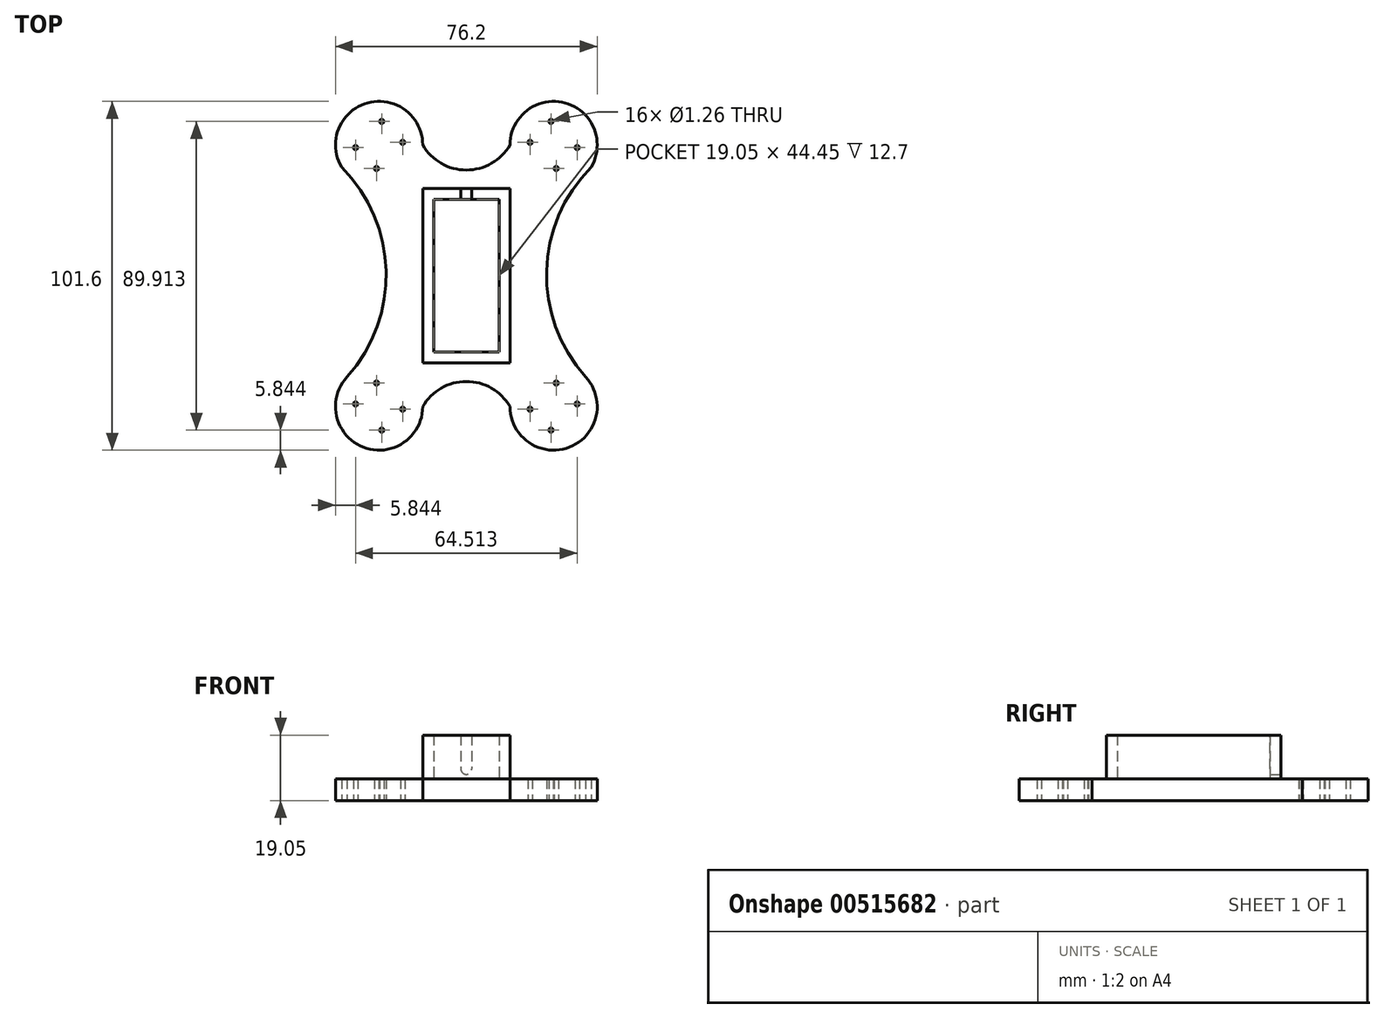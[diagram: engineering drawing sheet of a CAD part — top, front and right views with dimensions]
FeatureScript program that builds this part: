
annotation { "Feature Type Name" : "Feature", "Feature Type Description" : "" }
export const myFeature = defineFeature(function(context is Context, id is Id, definition is map)
    precondition{}
    {
        {
            var Q0;
            Q0=qCreatedBy(makeId("Top.planeOp"),FACE);
            var sketch = newSketch(context, id + "F0", { "sketchPlane" : qUnion([Q0])});
            skCircle(sketch, "E0", {"center": v(-25.4, 38.1) * mm, "radius": 7.54 * mm, "construction": true});
            skLineSegment(sketch, "E1.bottom", {"start": v(25.4, 38.1) * mm, "end": v(-25.4, 38.1) * mm, "construction": true});
            skLineSegment(sketch, "E1.top", {"start": v(25.4, -38.1) * mm, "end": v(-25.4, -38.1) * mm, "construction": true});
            skLineSegment(sketch, "E1.left", {"start": v(25.4, 38.1) * mm, "end": v(25.4, -38.1) * mm, "construction": true});
            skLineSegment(sketch, "E1.right", {"start": v(-25.4, 38.1) * mm, "end": v(-25.4, -38.1) * mm, "construction": true});
            skPoint(sketch, "E1.middle", {"position": v(0, 0) * mm});
            skArc(sketch, "E2", {"start": v(-12.7, 38.1) * mm, "mid": v(-28.75, 50.35) * mm, "end": v(-36.33, 31.64) * mm});
            skArc(sketch, "E3.MirrorC", {"start": v(12.7, 38.1) * mm, "mid": v(28.75, 50.35) * mm, "end": v(36.33, 31.64) * mm});
            skArc(sketch, "E4.MirrorC", {"start": v(12.7, -38.1) * mm, "mid": v(30.02, -49.93) * mm, "end": v(34.74, -29.5) * mm});
            skArc(sketch, "E5.MirrorC", {"start": v(-12.7, -38.1) * mm, "mid": v(-30.02, -49.93) * mm, "end": v(-34.74, -29.5) * mm});
            skArc(sketch, "E6", {"start": v(-34.9, -29.68) * mm, "mid": v(-23.37, 1.26) * mm, "end": v(-36.33, 31.64) * mm});
            skArc(sketch, "E7", {"start": v(-12.7, 38.1) * mm, "mid": v(0, 30.79) * mm, "end": v(12.7, 38.1) * mm});
            skArc(sketch, "E8.MirrorCS", {"start": v(34.9, -29.68) * mm, "mid": v(23.37, 1.26) * mm, "end": v(36.33, 31.64) * mm});
            skArc(sketch, "E9.MirrorCS", {"start": v(-12.7, -38.1) * mm, "mid": v(0, -30.79) * mm, "end": v(12.7, -38.1) * mm});
            skCircle(sketch, "E10", {"center": v(24.64, 44.96) * mm, "radius": 0.63 * mm});
            skCircle(sketch, "E11", {"center": v(18.54, 38.86) * mm, "radius": 0.63 * mm});
            skCircle(sketch, "E12", {"center": v(26.16, 31.24) * mm, "radius": 0.63 * mm});
            skCircle(sketch, "E13", {"center": v(32.26, 37.34) * mm, "radius": 0.63 * mm});
            skLineSegment(sketch, "E14", {"start": v(24.64, 44.96) * mm, "end": v(18.54, 38.86) * mm, "construction": true});
            skLineSegment(sketch, "E15", {"start": v(26.16, 31.24) * mm, "end": v(18.54, 38.86) * mm, "construction": true});
            skLineSegment(sketch, "E16", {"start": v(32.26, 37.34) * mm, "end": v(24.64, 44.96) * mm, "construction": true});
            skLineSegment(sketch, "E17", {"start": v(32.26, 37.34) * mm, "end": v(26.16, 31.24) * mm, "construction": true});
            skLineSegment(sketch, "E18", {"start": v(18.54, 38.86) * mm, "end": v(25.4, 38.1) * mm, "construction": true});
            skLineSegment(sketch, "E19", {"start": v(26.16, 31.24) * mm, "end": v(25.4, 38.1) * mm, "construction": true});
            skLineSegment(sketch, "E20", {"start": v(32.26, 37.34) * mm, "end": v(25.4, 38.1) * mm, "construction": true});
            skCircle(sketch, "E21.MirrorC", {"center": v(-18.54, 38.86) * mm, "radius": 0.63 * mm});
            skCircle(sketch, "E22.MirrorC", {"center": v(-24.64, 44.96) * mm, "radius": 0.63 * mm});
            skCircle(sketch, "E23.MirrorC", {"center": v(-32.26, 37.34) * mm, "radius": 0.63 * mm});
            skCircle(sketch, "E24.MirrorC", {"center": v(-26.16, 31.24) * mm, "radius": 0.63 * mm});
            skCircle(sketch, "E25.MirrorC", {"center": v(-32.26, -37.34) * mm, "radius": 0.63 * mm});
            skCircle(sketch, "E26.MirrorC", {"center": v(-26.16, -31.24) * mm, "radius": 0.63 * mm});
            skCircle(sketch, "E27.MirrorC", {"center": v(-18.54, -38.86) * mm, "radius": 0.63 * mm});
            skCircle(sketch, "E28.MirrorC", {"center": v(-24.64, -44.96) * mm, "radius": 0.63 * mm});
            skCircle(sketch, "E29.MirrorC", {"center": v(18.54, -38.86) * mm, "radius": 0.63 * mm});
            skCircle(sketch, "E30.MirrorC", {"center": v(24.64, -44.96) * mm, "radius": 0.63 * mm});
            skCircle(sketch, "E31.MirrorC", {"center": v(32.26, -37.34) * mm, "radius": 0.63 * mm});
            skCircle(sketch, "E32.MirrorC", {"center": v(26.16, -31.24) * mm, "radius": 0.63 * mm});
            skSolve(sketch);
        }
        {
            var Q0;
            Q0 = qSketchRegion(id + "F0", true);
            extrude(context, id + "F1", {"entities" : qUnion([Q0]), "depth" : 6.35 * mm, "offsetDistance" : 25.4 * mm});
        }
        {
            var Q0;
            Q0=makeQuery(id+"F1.opExtrude","CAP_FACE",FACE,{"disambiguationData":[OSD([sQuery(id+"F0.wireOp",EDGE,"E2"),sQuery(id+"F0.wireOp",EDGE,"E3.MirrorC"),sQuery(id+"F0.wireOp",EDGE,"E4.MirrorC"),sQuery(id+"F0.wireOp",EDGE,"E5.MirrorC"),sQuery(id+"F0.wireOp",EDGE,"E6"),sQuery(id+"F0.wireOp",EDGE,"E7"),sQuery(id+"F0.wireOp",EDGE,"E8.MirrorCS"),sQuery(id+"F0.wireOp",EDGE,"E9.MirrorCS"),sQuery(id+"F0.wireOp",EDGE,"E10"),sQuery(id+"F0.wireOp",EDGE,"E11"),sQuery(id+"F0.wireOp",EDGE,"E12"),sQuery(id+"F0.wireOp",EDGE,"E13"),sQuery(id+"F0.wireOp",EDGE,"E21.MirrorC"),sQuery(id+"F0.wireOp",EDGE,"E22.MirrorC"),sQuery(id+"F0.wireOp",EDGE,"E23.MirrorC"),sQuery(id+"F0.wireOp",EDGE,"E24.MirrorC"),sQuery(id+"F0.wireOp",EDGE,"E25.MirrorC"),sQuery(id+"F0.wireOp",EDGE,"E26.MirrorC"),sQuery(id+"F0.wireOp",EDGE,"E27.MirrorC"),sQuery(id+"F0.wireOp",EDGE,"E28.MirrorC"),sQuery(id+"F0.wireOp",EDGE,"E29.MirrorC"),sQuery(id+"F0.wireOp",EDGE,"E30.MirrorC"),sQuery(id+"F0.wireOp",EDGE,"E31.MirrorC"),sQuery(id+"F0.wireOp",EDGE,"E32.MirrorC")])],"isStart":false});
            var sketch = newSketch(context, id + "F2", { "sketchPlane" : qUnion([Q0])});
            skLineSegment(sketch, "E33.bottom", {"start": v(12.7, 25.4) * mm, "end": v(-12.7, 25.4) * mm});
            skLineSegment(sketch, "E33.top", {"start": v(12.7, -25.4) * mm, "end": v(-12.7, -25.4) * mm});
            skLineSegment(sketch, "E33.left", {"start": v(12.7, 25.4) * mm, "end": v(12.7, -25.4) * mm});
            skLineSegment(sketch, "E33.right", {"start": v(-12.7, 25.4) * mm, "end": v(-12.7, -25.4) * mm});
            skPoint(sketch, "E33.middle", {"position": v(0, 0) * mm});
            skLineSegment(sketch, "E34.bottom", {"start": v(9.53, 22.23) * mm, "end": v(-9.52, 22.23) * mm});
            skLineSegment(sketch, "E34.top", {"start": v(9.52, -22.23) * mm, "end": v(-9.53, -22.23) * mm});
            skLineSegment(sketch, "E34.left", {"start": v(9.53, 22.23) * mm, "end": v(9.52, -22.23) * mm});
            skLineSegment(sketch, "E34.right", {"start": v(-9.52, 22.23) * mm, "end": v(-9.53, -22.23) * mm});
            skLineSegment(sketch, "E35", {"start": v(0, 22.23) * mm, "end": v(0, 25.4) * mm, "construction": true});
            skLineSegment(sketch, "E36", {"start": v(-9.53, 13.4) * mm, "end": v(-12.7, 13.4) * mm, "construction": true});
            skSolve(sketch);
        }
        {
            var Q0;
            Q0 = qSketchRegion(id + "F2", true);
            extrude(context, id + "F3", {"entities" : qUnion([Q0]), "operationType" : NewBodyOperationType.ADD, "depth" : 12.7 * mm, "offsetDistance" : 25.4 * mm});
        }
        {
            var Q0;
            Q0=makeQuery(id+"F3.opExtrude","SWEPT_FACE",FACE,{"disambiguationData":[OSD([sQuery(id+"F2.wireOp",EDGE,"E33.bottom")])]});
            var sketch = newSketch(context, id + "F4", { "sketchPlane" : qUnion([Q0])});
            skLineSegment(sketch, "E37", {"start": v(-1.59, 19.05) * mm, "end": v(1.59, 19.05) * mm});
            skArc(sketch, "E38", {"start": v(-1.59, 9.2) * mm, "mid": v(0, 7.62) * mm, "end": v(1.59, 9.2) * mm});
            skLineSegment(sketch, "E39", {"start": v(-1.59, 19.05) * mm, "end": v(-1.59, 9.2) * mm});
            skLineSegment(sketch, "E40", {"start": v(1.59, 19.05) * mm, "end": v(1.59, 9.2) * mm});
            skLineSegment(sketch, "E41", {"start": v(1.59, 9.2) * mm, "end": v(0, 9.2) * mm, "construction": true});
            skLineSegment(sketch, "E42", {"start": v(-1.59, 9.2) * mm, "end": v(0, 9.2) * mm, "construction": true});
            skSolve(sketch);
        }
        {
            var Q0;
            Q0 = qSketchRegion(id + "F4", true);
            extrude(context, id + "F5", {"entities" : qUnion([Q0]), "operationType" : NewBodyOperationType.REMOVE, "oppositeDirection" : true, "depth" : 25.4 * mm, "offsetDistance" : 25.4 * mm});
        }
    });
